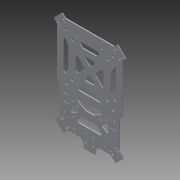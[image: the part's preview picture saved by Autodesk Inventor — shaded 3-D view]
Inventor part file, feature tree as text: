
AUTODESK INVENTOR PART (.ipt)
format: ipt  version: 2013 (Build 170138000, 138)  size: 6,376,448 bytes
history: native  units: mm
features: sketch x9, hole x5, extrude x4, other x2, fillet x1
ambient origin geometry x8: Origin, YZ Plane, XZ Plane, XY Plane, X Axis, Y Axis, Z Axis, Center Point
feature tree (21):
  other  "ソリッド1"
  extrude  "押し出し1"  Depth=115.0mm
  hole  "穴1"  [1 undecoded]
  hole  "穴2"  [1 undecoded]
  hole  "穴6"  [1 undecoded]
  hole  "穴7"  [1 undecoded]
  hole  "穴8"  [1 undecoded]
  extrude  "押し出し7"  TaperAngle=0.0deg  [1 undecoded]
  extrude  "押し出し8"  Depth=2.0mm TaperAngle=0.0deg
  extrude  "押し出し12"  Depth=3.2mm
  fillet  "フィレット1"  Radius=30.0mm
  sketch  "スケッチ1"
  sketch  "スケッチ2"
  sketch  "スケッチ3"
  sketch  "スケッチ9"
  sketch  "スケッチ11"
  sketch  "スケッチ12"
  sketch  "スケッチ13"
  sketch  "スケッチ14"
  sketch  "スケッチ17"
  other  "断面エッジを投影1"
note: 6 required parameter values undecoded (feature->parameter linkage not recoverable at this tier; creation-order binding heuristic only, values carry confidence <= 0.55)
